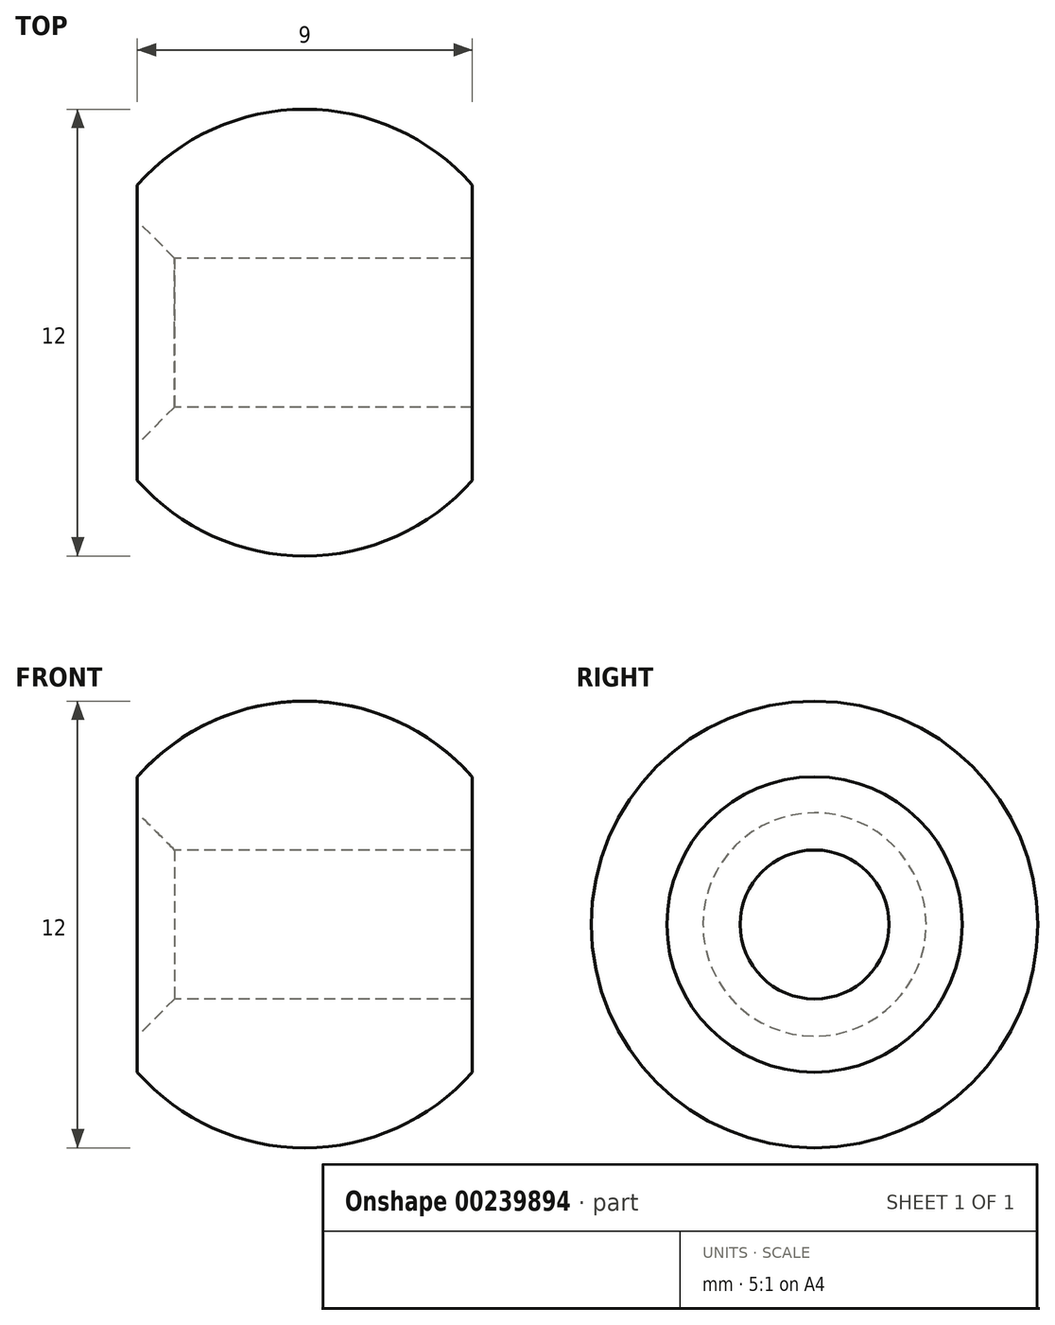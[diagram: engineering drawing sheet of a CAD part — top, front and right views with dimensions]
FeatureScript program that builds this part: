
annotation { "Feature Type Name" : "Feature", "Feature Type Description" : "" }
export const myFeature = defineFeature(function(context is Context, id is Id, definition is map)
    precondition{}
    {
        {
            var Q0;
            Q0=qCreatedBy(makeId("Front.planeOp"),FACE);
            var sketch = newSketch(context, id + "F0", { "sketchPlane" : qUnion([Q0])});
            skArc(sketch, "E0", {"start": v(4.5, 3.97) * mm, "mid": v(0, 6) * mm, "end": v(-4.5, 3.97) * mm});
            skLineSegment(sketch, "E1", {"start": v(-4.5, 3.97) * mm, "end": v(-4.5, 0) * mm});
            skLineSegment(sketch, "E2", {"start": v(-4.5, 0) * mm, "end": v(4.5, 0) * mm});
            skLineSegment(sketch, "E3", {"start": v(4.5, 0) * mm, "end": v(4.5, 3.97) * mm});
            skLineSegment(sketch, "E4", {"start": v(-10.42, 0) * mm, "end": v(12.71, 0) * mm, "construction": true});
            skSolve(sketch);
        }
        {
            var Q0;
            Q0=makeQuery(id+"F0.imprint","IMPRINT",FACE,{"disambiguationData":[TD([[makeQuery(id+"F0.imprint","IMPRINT",EDGE,{"derivedFrom":sQuery(id+"F0.wireOp",EDGE,"E0")}),1.0]])]});
            var Q1;
            Q1=sQuery(id+"F0.wireOp",EDGE,"E4");
            revolve(context, id + "F1", {"entities" : qUnion([Q0]), "axis" : qUnion([Q1]), "revolveType" : RevolveType.FULL});
        }
        {
            var Q0;
            Q0=makeQuery(id+"F1.opRevolve","SWEPT_FACE",FACE,{"disambiguationData":[OSD([sQuery(id+"F0.wireOp",EDGE,"E1")])]});
            var sketch = newSketch(context, id + "F2", { "sketchPlane" : qUnion([Q0])});
            skCircle(sketch, "E5", {"center": v(0, 0) * mm, "radius": 2 * mm});
            skSolve(sketch);
        }
        {
            var Q0;
            Q0=sQuery(id+"F2.wireOp",VERTEX,"E5.center");
            var Q1;
            Q1=makeQuery(id+"F1.opRevolve","SWEPT_BODY",BODY,{"disambiguationData":[OSD([sQuery(id+"F0.wireOp",EDGE,"E0"),sQuery(id+"F0.wireOp",EDGE,"E1"),sQuery(id+"F0.wireOp",EDGE,"E2"),sQuery(id+"F0.wireOp",EDGE,"E3")])]});
            hole(context, id + "F3", {"style" : HoleStyle.C_SINK, "endStyle" : HoleEndStyle.BLIND, "holeDiameter" : 4 * mm, "cSinkDiameter" : 6 * mm, "cSinkAngle" : 90 * degree, "holeDepth" : 10 * mm, "startFromSketch" : true, "locations" : qUnion([Q0]), "scope" : qUnion([Q1])});
        }
    });
